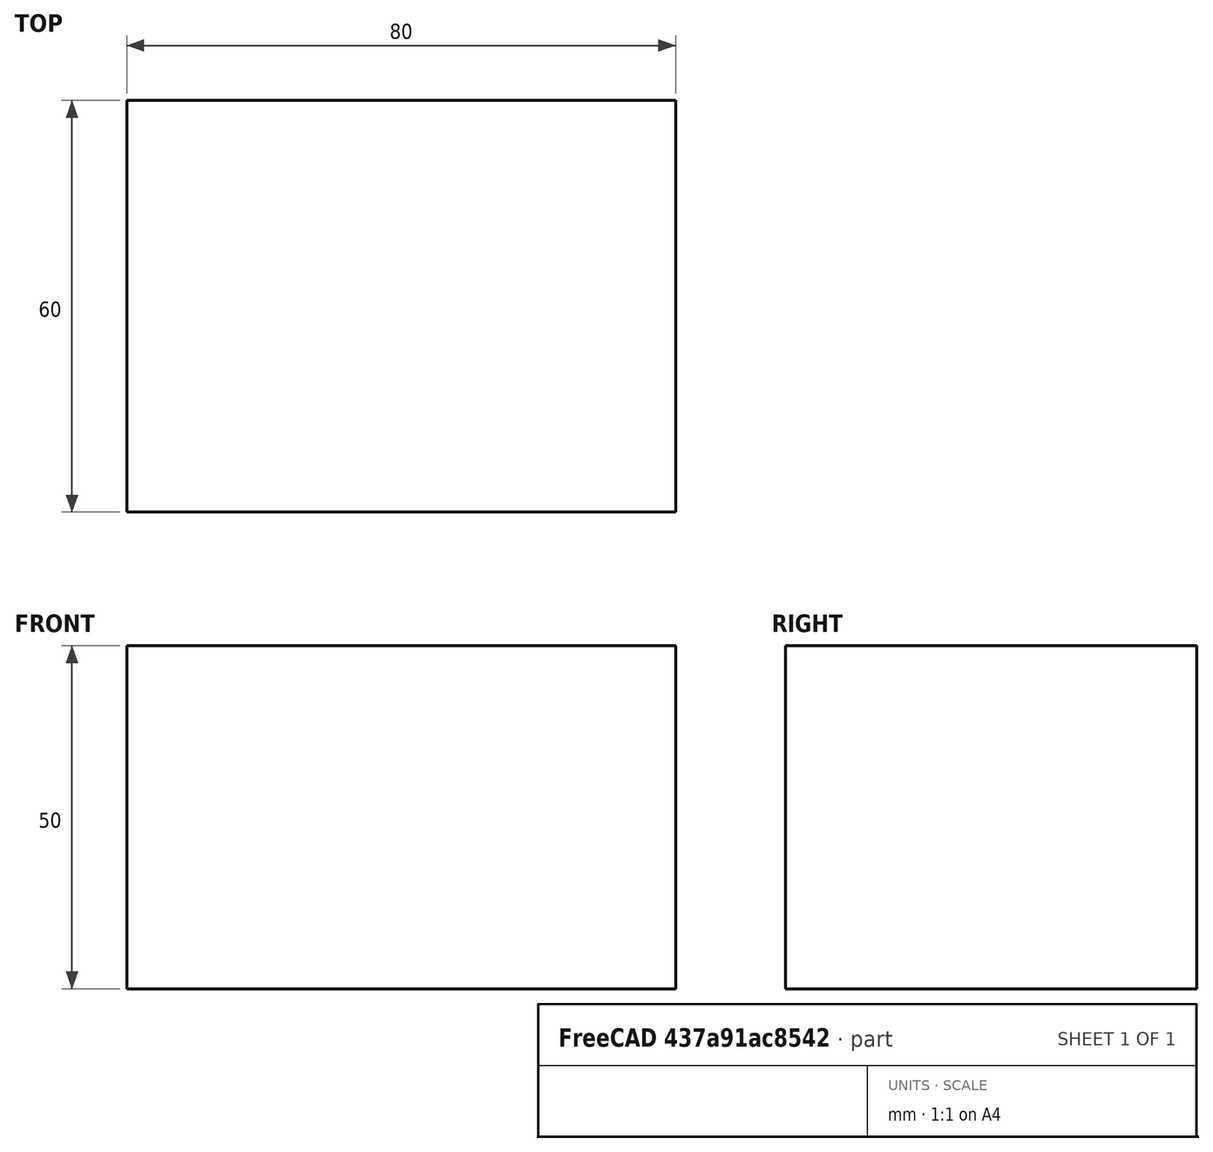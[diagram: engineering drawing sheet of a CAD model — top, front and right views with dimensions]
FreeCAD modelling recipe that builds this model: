
FCSTD DOCUMENT  (FreeCAD 0.15R4671 (Git))
Label: Flat Bar 80x60 EN10058 S235JR
License: All rights reserved
LicenseURL: http://en.wikipedia.org/wiki/All_rights_reserved
objects: Sketcher::SketchObject×1, Part::Extrusion×1
note: 2 computed .brp shape members not serialized (recipe doc carries the construction recipe); baked Part::Feature solids carry a one-line shape summary decoded from their .brp

FEATURE [Sketcher::SketchObject] Sketch
  sketch-geometry (4):
    g0: LineSegment StartX=-40 StartY=-30 StartZ=0 EndX=40 EndY=-30 EndZ=0
    g1: LineSegment StartX=40 StartY=-30 StartZ=0 EndX=40 EndY=30 EndZ=0
    g2: LineSegment StartX=40 StartY=30 StartZ=0 EndX=-40 EndY=30 EndZ=0
    g3: LineSegment StartX=-40 StartY=30 StartZ=0 EndX=-40 EndY=-30 EndZ=0
  constraints (12):
    c: Coincident(g0,g1)
    c: Coincident(g1,g2)
    c: Coincident(g2,g3)
    c: Coincident(g3,g0)
    c: Horizontal(g0)
    c: Horizontal(g2)
    c: Vertical(g1)
    c: Vertical(g3)
    c: Symmetric(g1,g2,g-2)
    c: Symmetric(g0,g1,g-1)
    c: DistanceY(g1) = 60
    c: DistanceX(g0) = 80
FEATURE [Part::Extrusion] Extrude  label="Flat Bar 80x60 EN10058 S235JR"
  Base = -> Sketch
  Dir = (0,0,50)
  Solid = true
